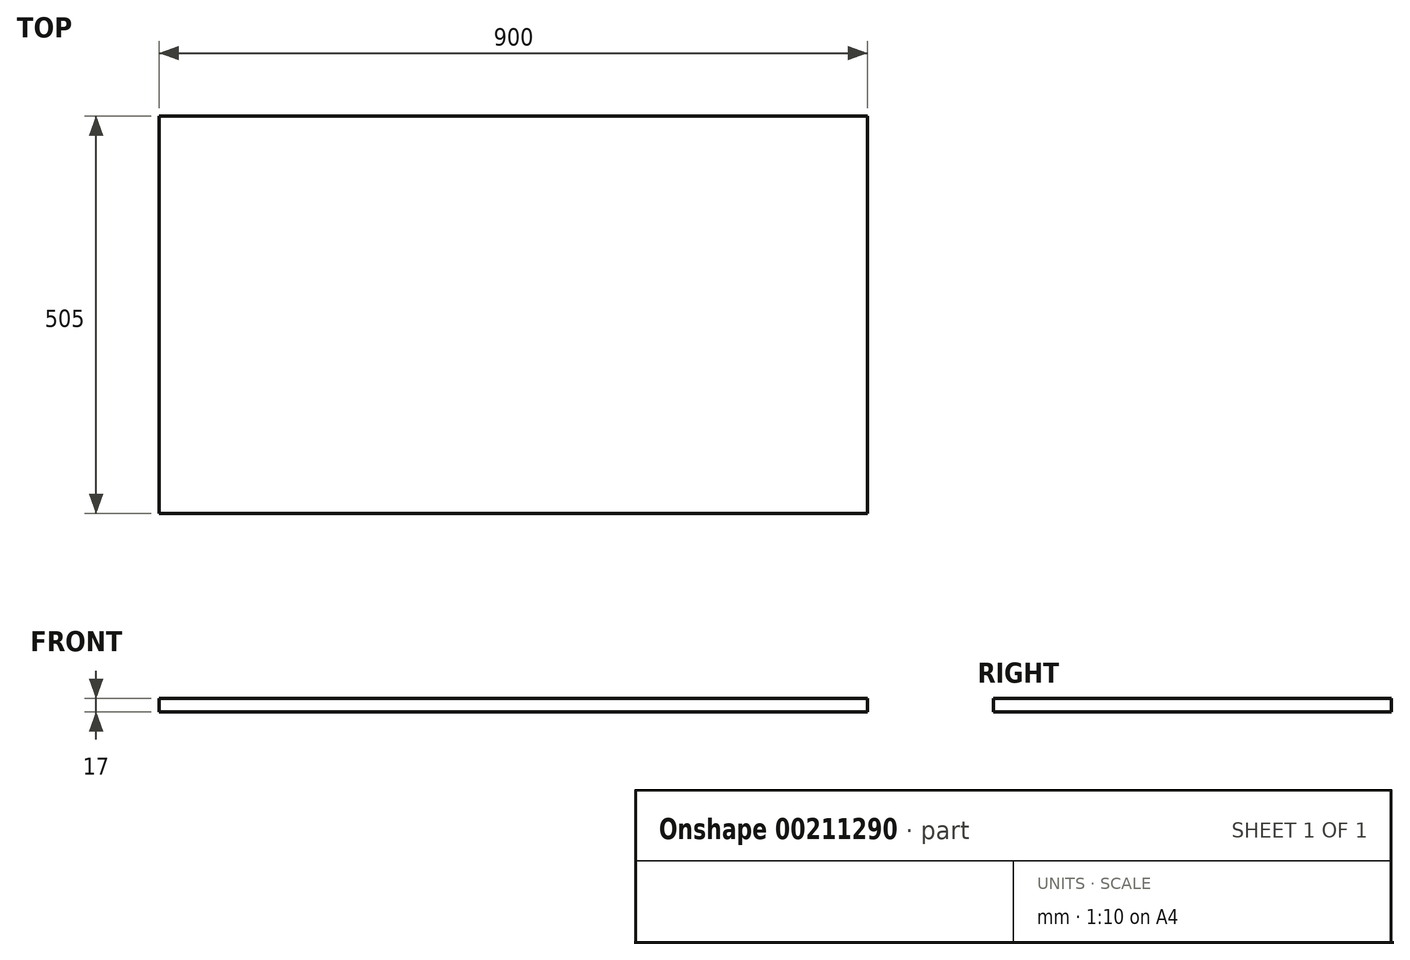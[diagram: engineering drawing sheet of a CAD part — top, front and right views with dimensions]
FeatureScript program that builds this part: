
annotation { "Feature Type Name" : "Feature", "Feature Type Description" : "" }
export const myFeature = defineFeature(function(context is Context, id is Id, definition is map)
    precondition{}
    {
        {
            var Q0;
            Q0=qCreatedBy(makeId("Top.planeOp"),FACE);
            var sketch = newSketch(context, id + "F0", { "sketchPlane" : qUnion([Q0])});
            skLineSegment(sketch, "E0.bottom", {"start": v(-56.26, 480.58) * mm, "end": v(843.74, 480.58) * mm});
            skLineSegment(sketch, "E0.top", {"start": v(-56.26, -24.42) * mm, "end": v(843.74, -24.42) * mm});
            skLineSegment(sketch, "E0.left", {"start": v(-56.26, 480.58) * mm, "end": v(-56.26, -24.42) * mm});
            skLineSegment(sketch, "E0.right", {"start": v(843.74, 480.58) * mm, "end": v(843.74, -24.42) * mm});
            skSolve(sketch);
        }
        {
            var Q0;
            Q0=makeQuery(id+"F0.imprint","IMPRINT",FACE,{"disambiguationData":[TD([[makeQuery(id+"F0.imprint","IMPRINT",EDGE,{"derivedFrom":sQuery(id+"F0.wireOp",EDGE,"E0.bottom")}),-1.0]])]});
            extrude(context, id + "F1", {"entities" : qUnion([Q0]), "depth" : 17 * mm});
        }
    });
